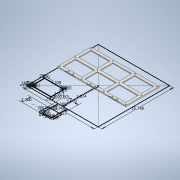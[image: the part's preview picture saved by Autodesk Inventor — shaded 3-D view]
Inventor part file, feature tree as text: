
AUTODESK INVENTOR PART (.ipt)
format: ipt  version: 2020 (Build 240168000, 168)  size: 355,840 bytes
history: native  units: in
note: dims shown in document units (in); Inventor stores cm internally (conversion verified against a paired STEP export)
features: sketch x6, extrude x6, hole x3, pattern_linear x1
ambient origin geometry x8: Origin, YZ Plane, XZ Plane, XY Plane, X Axis, Y Axis, Z Axis, Center Point
bodies: Solid1 (feature_tree)
feature tree (16):
  sketch  "Sketch1"  dims[d0=3.0in d1=2.0in]
  extrude  "Extrusion1"  Depth=2.0in
  hole  "Hole1"  [1 undecoded]
  sketch  "Sketch2"  dims[d2=0.25in d3=1.0in]
  extrude  "Extrusion2"  TaperAngle=0.0deg  [1 undecoded]
  hole  "Hole2"  [1 undecoded]
  extrude  "Extrusion3"  Depth=0.25in
  pattern_linear  "Rectangular Pattern1"  Spacing1=90.0deg  [1 undecoded]
  extrude  "Extrusion4"  Depth=0.25in
  extrude  "Extrusion5"  Depth=0.25in
  extrude  "Extrusion6"  Depth=0.25in
  hole  "Hole3"  [1 undecoded]
  sketch  "Sketch3"  dims[d4=1.0in d5=0.0in]
  sketch  "Sketch4"  dims[d6=0.5in d7=0.5in]
  sketch  "Sketch5"  dims[d8=0.25in d9=0.25in]
  sketch  "Sketch6"  dims[d10=2.9528in d11=90.0deg d12=2.9528in d13=1.0in d14=7.874in d15=90.0deg d16=15.748in d17=15.748in d18=0.25in d19=0.0in d20=0.26in d21=0.5in d22=0.375in d23=0.25in d24=0.5635in d25=1.0in d26=0.8108in d27=0.25in d28=90.0deg d29=0.25in d30=0.25in d31=0.25in d32=4.3386in d33=2.9134in d34=0.25in d35=0.25in d36=0.25in d37=0.25in d38=0.25in d39=0.315in d40=90.0deg d41=0.0787in d42=0.0787in d43=0.0787in d44=0.0787in d45=0.0in d46=0.0in d47=0.203in d48=0.625in d49=0.375in d50=0.25in d51=0.5635in d52=1.0in d53=0.8108in d54=0.0787in d55=0.0in d56=1.1811in d58=4.839in d59=1.5748in d61=3.423in d62=0.25in d63=0.25in d64=0.0in d65=0.0in d66=1.0in d67=0.0in d68=0.125in d69=2.0in d70=0.125in d71=2.0in d72=0.125in d73=0.125in d74=2.0in d75=0.125in d76=0.0in d77=0.25in d78=0.5in d79=1.0in d80=0.5in d81=1.0in d82=1.0in d83=0.25in d84=0.5in d85=90.0deg d86=0.266in d87=0.75in d88=0.438in d89=0.25in d90=0.5635in d91=1.0in d92=0.8108in]
note: 5 required parameter values undecoded (feature->parameter linkage not recoverable at this tier; creation-order binding heuristic only, values carry confidence <= 0.55)
